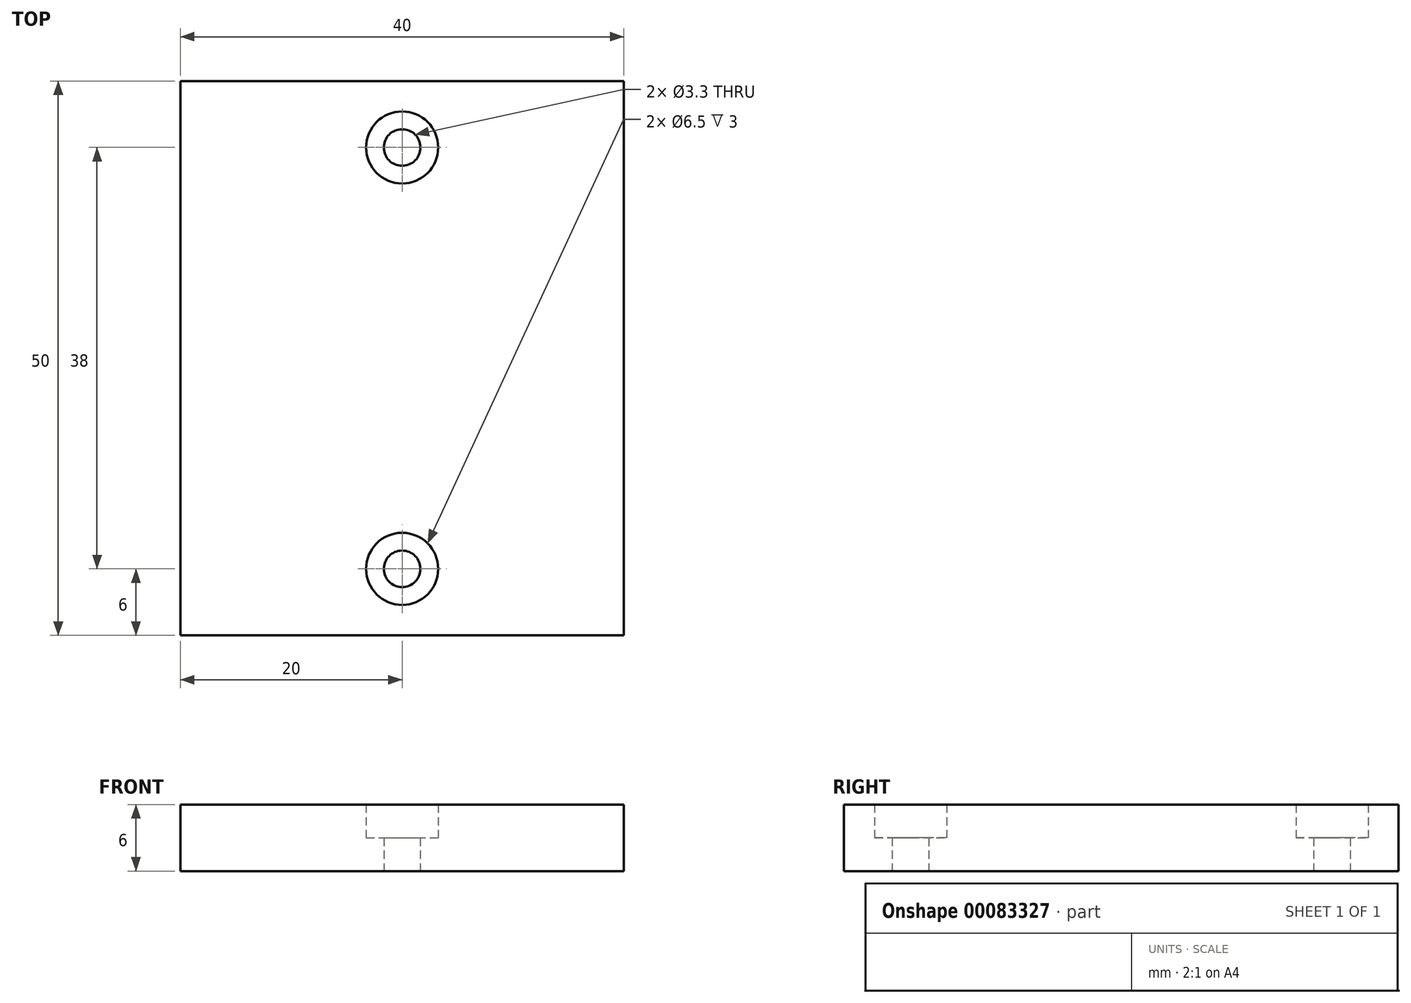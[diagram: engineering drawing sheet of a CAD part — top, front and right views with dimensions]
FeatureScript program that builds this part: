
annotation { "Feature Type Name" : "Feature", "Feature Type Description" : "" }
export const myFeature = defineFeature(function(context is Context, id is Id, definition is map)
    precondition{}
    {
        {
            assignVariable(context, id + "F0", {"name" : "BaseHeight", "anyValue" : 6});
        }
        {
            var Q0;
            Q0=qCreatedBy(makeId("Top.planeOp"),FACE);
            var sketch = newSketch(context, id + "F1", { "sketchPlane" : qUnion([Q0])});
            skLineSegment(sketch, "E0.bottom", {"start": v(-20, 25) * mm, "end": v(20, 25) * mm});
            skLineSegment(sketch, "E0.top", {"start": v(-20, -25) * mm, "end": v(20, -25) * mm});
            skLineSegment(sketch, "E0.left", {"start": v(-20, 25) * mm, "end": v(-20, -25) * mm});
            skLineSegment(sketch, "E0.right", {"start": v(20, 25) * mm, "end": v(20, -25) * mm});
            skPoint(sketch, "E0.middle", {"position": v(0, 0) * mm});
            skPoint(sketch, "E1", {"position": v(0, 19) * mm});
            skLineSegment(sketch, "E2", {"start": v(-20, 0) * mm, "end": v(20, 0) * mm, "construction": true});
            skPoint(sketch, "E3.MirrorP", {"position": v(0, -19) * mm});
            skLineSegment(sketch, "E4", {"start": v(0, 0) * mm, "end": v(0, 25) * mm, "construction": true});
            skLineSegment(sketch, "E5.MirrorCS", {"start": v(0, 0) * mm, "end": v(0, -25) * mm, "construction": true});
            skSolve(sketch);
        }
        {
            var Q0;
            Q0=makeQuery(id+"F1.imprint","IMPRINT",FACE,{"disambiguationData":[TD([[makeQuery(id+"F1.imprint","IMPRINT",EDGE,{"derivedFrom":sQuery(id+"F1.wireOp",EDGE,"E0.bottom")}),-1.0]])]});
            extrude(context, id + "F2", {"entities" : qUnion([Q0]), "oppositeDirection" : true, "depth" : (getVariable(context, 'BaseHeight')) * mm});
        }
        {
            var Q0;
            Q0=sQuery(id+"F1.wireOp",VERTEX,"E3.MirrorP");
            var Q1;
            Q1=sQuery(id+"F1.wireOp",VERTEX,"E1");
            var Q2;
            Q2=makeQuery(id+"F2.opExtrude","SWEPT_BODY",BODY,{"disambiguationData":[OSD([sQuery(id+"F1.wireOp",EDGE,"E0.bottom"),sQuery(id+"F1.wireOp",EDGE,"E0.top"),sQuery(id+"F1.wireOp",EDGE,"E0.left"),sQuery(id+"F1.wireOp",EDGE,"E0.right")])]});
            hole(context, id + "F3", {"style" : HoleStyle.C_BORE, "endStyle" : HoleEndStyle.THROUGH, "standardTappedOrClearance" : lookupTablePath({ "standard" : "ISO", "fit" : "Normal", "size" : "M3", "type" : "Clearance" }), "standardBlindInLast" : lookupTablePath({ "fit" : "Standard", "standard" : "ISO", "size" : "M3", "type" : "Clearance" }), "holeDiameter" : 3.3 * mm, "cBoreDiameter" : 6.5 * mm, "cBoreDepth" : 3 * mm, "locations" : qUnion([Q0, Q1]), "scope" : qUnion([Q2]), "isTappedThrough" : true, "startStyle" : HoleStartStyle.SKETCH});
        }
    });
